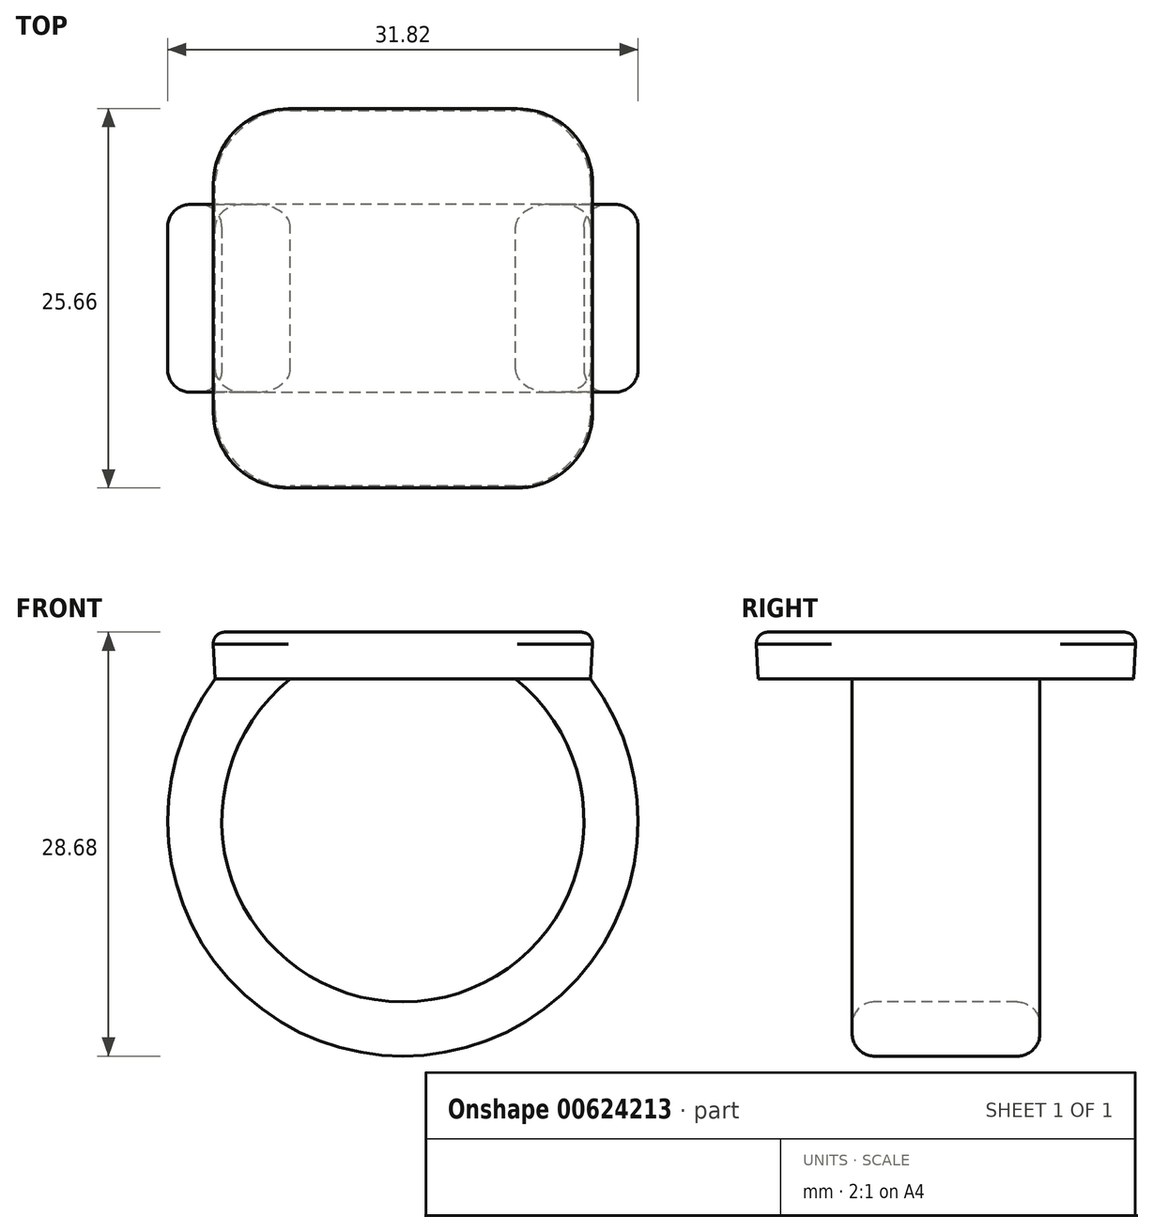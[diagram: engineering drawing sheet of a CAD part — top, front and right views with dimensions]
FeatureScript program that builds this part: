
annotation { "Feature Type Name" : "Feature", "Feature Type Description" : "" }
export const myFeature = defineFeature(function(context is Context, id is Id, definition is map)
    precondition{}
    {
        {
            var Q0;
            Q0=qCreatedBy(makeId("Top.planeOp"),FACE);
            var sketch = newSketch(context, id + "F0", { "sketchPlane" : qUnion([Q0])});
            skLineSegment(sketch, "E0.bottom", {"start": v(-12.7, 12.7) * mm, "end": v(12.7, 12.7) * mm});
            skLineSegment(sketch, "E0.top", {"start": v(-12.7, -12.7) * mm, "end": v(12.7, -12.7) * mm});
            skLineSegment(sketch, "E0.left", {"start": v(-12.7, 12.7) * mm, "end": v(-12.7, -12.7) * mm});
            skLineSegment(sketch, "E0.right", {"start": v(12.7, 12.7) * mm, "end": v(12.7, -12.7) * mm});
            skPoint(sketch, "E0.middle", {"position": v(0, 0) * mm});
            skSolve(sketch);
        }
        {
            var Q0;
            Q0 = qSketchRegion(id + "F0", true);
            extrude(context, id + "F1", {"entities" : qUnion([Q0]), "depth" : 3.17 * mm, "offsetDistance" : 25.4 * mm, "hasDraft" : true, "draftAngle" : 3 * degree});
        }
        {
            var Q0;
            Q0=qCreatedBy(makeId("Front.planeOp"),FACE);
            var sketch = newSketch(context, id + "F2", { "sketchPlane" : qUnion([Q0])});
            skArc(sketch, "E1", {"start": v(-10.16, 0) * mm, "mid": v(0, -23.56) * mm, "end": v(10.16, 0) * mm});
            skSolve(sketch);
        }
        {
            var Q0;
            Q0=makeQuery(id+"F1.opExtrude","CAP_FACE",FACE,{"disambiguationData":[OSD([sQuery(id+"F0.wireOp",EDGE,"E0.bottom"),sQuery(id+"F0.wireOp",EDGE,"E0.top"),sQuery(id+"F0.wireOp",EDGE,"E0.left"),sQuery(id+"F0.wireOp",EDGE,"E0.right")])],"isStart":true});
            var sketch = newSketch(context, id + "F3", { "sketchPlane" : qUnion([Q0])});
            skLineSegment(sketch, "E2.bottom", {"start": v(-12.7, 6.35) * mm, "end": v(-7.62, 6.35) * mm});
            skLineSegment(sketch, "E2.top", {"start": v(-12.7, -6.35) * mm, "end": v(-7.62, -6.35) * mm});
            skLineSegment(sketch, "E2.left", {"start": v(-12.7, 6.35) * mm, "end": v(-12.7, -6.35) * mm});
            skLineSegment(sketch, "E2.right", {"start": v(-7.62, 6.35) * mm, "end": v(-7.62, -6.35) * mm});
            skPoint(sketch, "E2.middle", {"position": v(-10.16, 0) * mm});
            skSolve(sketch);
        }
        {
            var Q0;
            Q0 = qSketchRegion(id + "F3", true);
            var Q1;
            Q1 = qConstructionFilter(qBodyType(qCreatedBy(id + "F2" ,EDGE), BodyType.WIRE), ConstructionObject.NO);
            sweep(context, id + "F4", {"operationType" : NewBodyOperationType.ADD, "profiles" : qUnion([Q0]), "path" : qUnion([Q1])});
        }
        {
            var Q0;
            Q0=qCreatedBy(makeId("Front.planeOp"),FACE);
            var sketch = newSketch(context, id + "F5", { "sketchPlane" : qUnion([Q0])});
            skLineSegment(sketch, "E3.0", {"start": v(7.62, 0) * mm, "end": v(10.16, 0) * mm});
            skArc(sketch, "E3.1", {"start": v(10.01, -2.54) * mm, "mid": v(8.9, -1.18) * mm, "end": v(7.62, 0) * mm});
            skLineSegment(sketch, "E3.2", {"start": v(10.01, -2.54) * mm, "end": v(10.16, 0) * mm});
            skPoint(sketch, "E4.orphan", {"position": v(-7.62, 0) * mm});
            skPoint(sketch, "E5.orphan", {"position": v(-12.7, 0) * mm});
            skPoint(sketch, "E6.orphan", {"position": v(12.7, 0) * mm});
            skSolve(sketch);
        }
        {
            var Q0;
            Q0=makeQuery(id+"F5.imprint","IMPRINT",FACE,{"disambiguationData":[TD([[makeQuery(id+"F5.imprint","IMPRINT",EDGE,{"derivedFrom":sQuery(id+"F5.wireOp",EDGE,"E3.0")}),-1.0]])]});
            var Q1;
            Q1=makeQuery(id+"F4.opSweep","SWEPT_FACE",FACE,{"disambiguationData":[OSD([sQuery(id+"F2.wireOp",EDGE,"E1"),sQuery(id+"F3.wireOp",EDGE,"E2.bottom")])]});
            var Q2;
            Q2=makeQuery(id+"F4.opSweep","SWEPT_FACE",FACE,{"disambiguationData":[OSD([sQuery(id+"F2.wireOp",EDGE,"E1"),sQuery(id+"F3.wireOp",EDGE,"E2.top")])]});
            extrude(context, id + "F6", {"entities" : qUnion([Q0]), "operationType" : NewBodyOperationType.ADD, "endBound" : BoundingType.UP_TO_SURFACE, "depth" : 25.4 * mm, "endBoundEntityFace" : qUnion([Q1]), "offsetDistance" : 25.4 * mm, "hasSecondDirection" : true, "secondDirectionBound" : SecondDirectionBoundingType.UP_TO_SURFACE, "secondDirectionOppositeDirection" : true, "secondDirectionDepth" : 25.4 * mm, "secondDirectionBoundEntityFace" : qUnion([Q2])});
        }
        {
            var Q0;
            Q0=makeQuery(id+"F1.opExtrude","SWEPT_EDGE",EDGE,{"disambiguationData":[OSD([sQuery(id+"F0.wireOp",EDGE,"E0.bottom"),sQuery(id+"F0.wireOp",EDGE,"E0.left")])]});
            var Q1;
            Q1=makeQuery(id+"F1.opExtrude","SWEPT_EDGE",EDGE,{"disambiguationData":[OSD([sQuery(id+"F0.wireOp",EDGE,"E0.top"),sQuery(id+"F0.wireOp",EDGE,"E0.left")])]});
            var Q2;
            Q2=makeQuery(id+"F1.opExtrude","SWEPT_EDGE",EDGE,{"disambiguationData":[OSD([sQuery(id+"F0.wireOp",EDGE,"E0.bottom"),sQuery(id+"F0.wireOp",EDGE,"E0.right")])]});
            var Q3;
            Q3=makeQuery(id+"F1.opExtrude","SWEPT_EDGE",EDGE,{"disambiguationData":[OSD([sQuery(id+"F0.wireOp",EDGE,"E0.top"),sQuery(id+"F0.wireOp",EDGE,"E0.right")])]});
            fillet(context, id + "F7", {"entities" : qUnion([Q0, Q1, Q2, Q3]), "radius" : 5.08 * mm, "tangentPropagation" : true, "allowEdgeOverflow" : false});
        }
        {
            var Q0;
            Q0=makeQuery(id+"F4.opSweep","SWEPT_EDGE",EDGE,{"disambiguationData":[OSD([sQuery(id+"F0.wireOp",EDGE,"E0.left"),sQuery(id+"F2.wireOp",EDGE,"E1"),sQuery(id+"F3.wireOp",EDGE,"E2.bottom"),sQuery(id+"F3.wireOp",EDGE,"E2.left")])]});
            var Q1;
            {var subQ0=sQuery(id+"F3.wireOp",EDGE,"E2.bottom");var subQ1=sQuery(id+"F2.wireOp",EDGE,"E1");Q1=makeQuery(id+"F6.boolean.opBoolean","MERGE",EDGE,{"derivedFrom":[makeQuery(id+"F4.opSweep","SWEPT_EDGE",EDGE,{"disambiguationData":[OSD([subQ1,subQ0,sQuery(id+"F3.wireOp",EDGE,"E2.right")])]}),makeQuery(id+"F6.opExtrude","TWEAK_EDGE",EDGE,{"derivedFrom":[makeQuery(id+"F4.opSweep","SWEPT_FACE",FACE,{"disambiguationData":[OSD([subQ1,subQ0])]}),makeQuery(id+"F5.imprint","IMPRINT",EDGE,{"derivedFrom":sQuery(id+"F5.wireOp",EDGE,"E3.1")})]})]});}
            var Q2;
            {var subQ0=sQuery(id+"F3.wireOp",EDGE,"E2.top");var subQ1=sQuery(id+"F2.wireOp",EDGE,"E1");Q2=makeQuery(id+"F6.boolean.opBoolean","MERGE",EDGE,{"derivedFrom":[makeQuery(id+"F4.opSweep","SWEPT_EDGE",EDGE,{"disambiguationData":[OSD([subQ1,subQ0,sQuery(id+"F3.wireOp",EDGE,"E2.right")])]}),makeQuery(id+"F6.opExtrude","TWEAK_EDGE",EDGE,{"derivedFrom":[makeQuery(id+"F4.opSweep","SWEPT_FACE",FACE,{"disambiguationData":[OSD([subQ1,subQ0])]}),makeQuery(id+"F5.imprint","IMPRINT",EDGE,{"derivedFrom":sQuery(id+"F5.wireOp",EDGE,"E3.1")})]})]});}
            var Q3;
            Q3=makeQuery(id+"F4.opSweep","SWEPT_EDGE",EDGE,{"disambiguationData":[OSD([sQuery(id+"F0.wireOp",EDGE,"E0.left"),sQuery(id+"F2.wireOp",EDGE,"E1"),sQuery(id+"F3.wireOp",EDGE,"E2.top"),sQuery(id+"F3.wireOp",EDGE,"E2.left")])]});
            fillet(context, id + "F8", {"entities" : qUnion([Q0, Q1, Q2, Q3]), "radius" : 1.52 * mm, "tangentPropagation" : true, "allowEdgeOverflow" : false});
        }
        {
            var Q0;
            Q0=makeQuery(id+"F1.opExtrude","CAP_FACE",FACE,{"disambiguationData":[OSD([sQuery(id+"F0.wireOp",EDGE,"E0.bottom"),sQuery(id+"F0.wireOp",EDGE,"E0.top"),sQuery(id+"F0.wireOp",EDGE,"E0.left"),sQuery(id+"F0.wireOp",EDGE,"E0.right")])],"isStart":false});
            fillet(context, id + "F9", {"entities" : qUnion([Q0]), "radius" : 0.76 * mm, "tangentPropagation" : true, "allowEdgeOverflow" : false});
        }
    });
